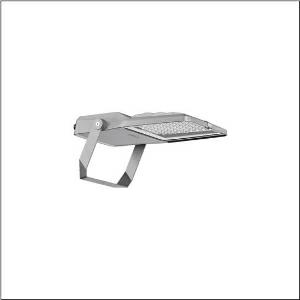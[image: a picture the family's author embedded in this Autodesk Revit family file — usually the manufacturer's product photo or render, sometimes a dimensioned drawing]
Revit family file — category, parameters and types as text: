
# Revit family: floodlight_fl_21_mini___pl61_5xa7773c4c1a_fa47
name_source: partatom
category: Lighting Fixtures
units: mm (PartAtom-declared; Revit-internal decimal feet)

## family parameters
Cut with Voids When Loaded = No
Host = Face
Light Source = No
Part Type = Normal
Room Calculation Point = No
Round Connector Dimension = Use Diameter
Shared = No

## types (1)
- --- (1 x LED, 19990 lm, 163.5 W, 4000K)
    Apparent Load = 163 VA
    CIE Flux Codes = 33 65 98 100 100
    Color Rendering = 70
    Color Temperature = 4000K
    Default Elevation = 1800 mm
    Description = Floodlight FL 21 mini, floodlight, primary light control with lens, of PMMA, primary optical cover: protective disc, of toughened safety glass, transparent, light distribution: PL61, light emission: direct distribution, installation type: surface-mounted, LED, High Power LED, rated luminous flux: 19.990lm, luminous efficacy: 122lm/W, light colour: 740, colour temperature: 4000K, control gear: ON/OFF Multilumen, control: Temp-Guard, with terminal, 6-pole, mains connection: 220..240V, AC, 50/60Hz, start of lifetime: 164W, luminaire housing, of diecast aluminium, powder-coated, Siteco® metallic grey (DB 702S), corrosivity category C5 mid according to DIN EN ISO 12944, suitable for swimming pools, chlorine-resistant, sealing non-destructively replaceable, mounting bracket, of steel, galvanised, powder-coated, Siteco® metallic grey (DB 702S), ON/OFF, protection rating (complete): IP66, insulation class (complete): insulation class I (protective earthing), certification: CE, ENEC, VDE, protection symbol: D, impact resistance: IK08, permissible operating ambient temperature: -40..+40°C, permissible operating ambient temperature for outdoor applications: -40..+50°C, standard: DIN EN 12944, LABS conformity tested according to VDMA 24364:2018-05, packaging unit: 1 piece

Light Distribution: PL61
    Height = 70 mm
    Lamp = 1 x LED
    Lamp Light Flux = 19990 lm
    Lamp Power = 163.5 W
    Lamp count = 1
    Length = 485 mm
    Luminous efficacy = 122 lm/W
    Manufacturer = Siteco
    ModVariant = No
    Model = 5XA7773C4C1A
    Number of Poles = 1
    OnlyDefault = Yes
    Power Factor = 1
    Product Name = Floodlight FL 21 mini | PL61
    Product group = floodlight | pylon annexe
    ProductGroupID = 6201
    Protection Class = Protection class I
    Protection Degree = IP 66
    RLX_Detail_Level = 1
    RLX_Emergency_Light_Flux = 0 lm
    RLX_Emergency_Type = 0
    RLX_Emergency_Type_DB = No
    RlxData = <blob elided: 94369 chars, md5=f731a4a9>
    Socket = socket
    Standby Power = 0 W
    System Light Flux = 19990 lm
    System Power = 163 W
    Type Comments = factory setting: luminous flux: 100 % | (ON | - | - | - | - | - | - | -) | 825 mA
    Type Image = l_1006845.jpg
    URL = http://relux.com
    VarID = @adj_194305
    Voltage = 0 V
    Weight = 0.00 kg
    Width = 337 mm

## geometry (parser evidence)
native form markers: Blend x4, Sweep x15
no freeform markers — native parametric forms only
